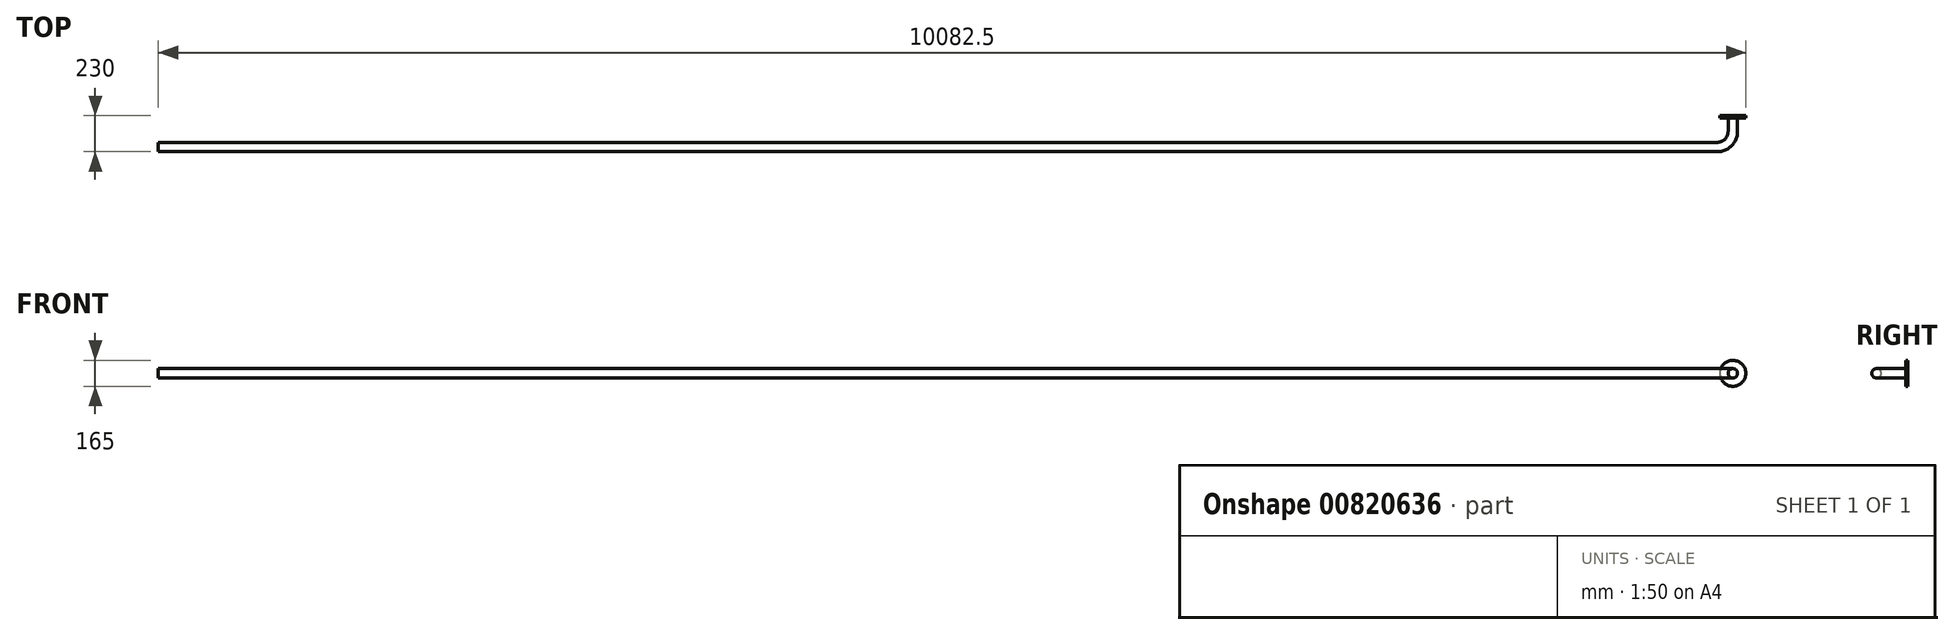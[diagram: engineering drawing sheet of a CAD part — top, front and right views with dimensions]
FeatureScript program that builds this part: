
annotation { "Feature Type Name" : "Feature", "Feature Type Description" : "" }
export const myFeature = defineFeature(function(context is Context, id is Id, definition is map)
    precondition{}
    {
        {
            var Q0;
            Q0=qCreatedBy(makeId("Top.planeOp"),FACE);
            var sketch = newSketch(context, id + "F0", { "sketchPlane" : qUnion([Q0])});
            skLineSegment(sketch, "E0", {"start": v(-10000, 0) * mm, "end": v(-100, 0) * mm});
            skLineSegment(sketch, "E1", {"start": v(0, 100) * mm, "end": v(0, 200) * mm});
            skPoint(sketch, "E2.visualSharp", {"position": v(0, 0) * mm});
            skArc(sketch, "E2.filletArc", {"start": v(-100, 0) * mm, "mid": v(-29.29, 29.29) * mm, "end": v(0, 100) * mm});
            skSolve(sketch);
        }
        {
            var Q0;
            Q0=qCreatedBy(makeId("Front.planeOp"),FACE);
            cPlane(context, id + "F1", {"entities" : qUnion([Q0]), "cplaneType" : CPlaneType.OFFSET, "offset" : 200 * mm, "oppositeDirection" : true, "width" : 150 * mm, "height" : 150 * mm});
        }
        {
            var Q0;
            Q0=qCreatedBy(id+"F1.planeOp",FACE);
            var sketch = newSketch(context, id + "F2", { "sketchPlane" : qUnion([Q0])});
            skCircle(sketch, "E3", {"center": v(0, 0) * mm, "radius": 30 * mm});
            skCircle(sketch, "E4", {"center": v(0, 0) * mm, "radius": 82.5 * mm});
            skSolve(sketch);
        }
        {
            var Q0;
            Q0=makeQuery(id+"F2.imprint","IMPRINT",FACE,{"disambiguationData":[TD([[makeQuery(id+"F2.imprint","IMPRINT",EDGE,{"derivedFrom":sQuery(id+"F2.wireOp",EDGE,"E3")}),1.0]])]});
            var Q1;
            Q1=sQuery(id+"F0.wireOp",EDGE,"E1");
            var Q2;
            Q2=sQuery(id+"F0.wireOp",EDGE,"E2.filletArc");
            var Q3;
            Q3=sQuery(id+"F0.wireOp",EDGE,"E0");
            sweep(context, id + "F3", {"profiles" : qUnion([Q0]), "path" : qUnion([Q1, Q2, Q3])});
        }
        {
            var Q0;
            Q0=makeQuery(id+"F2.imprint","IMPRINT",FACE,{"disambiguationData":[TD([[makeQuery(id+"F2.imprint","IMPRINT",EDGE,{"derivedFrom":sQuery(id+"F2.wireOp",EDGE,"E3")}),-1.0]])]});
            extrude(context, id + "F4", {"entities" : qUnion([Q0]), "operationType" : NewBodyOperationType.ADD, "depth" : 15 * mm, "offsetDistance" : 25 * mm});
        }
    });
